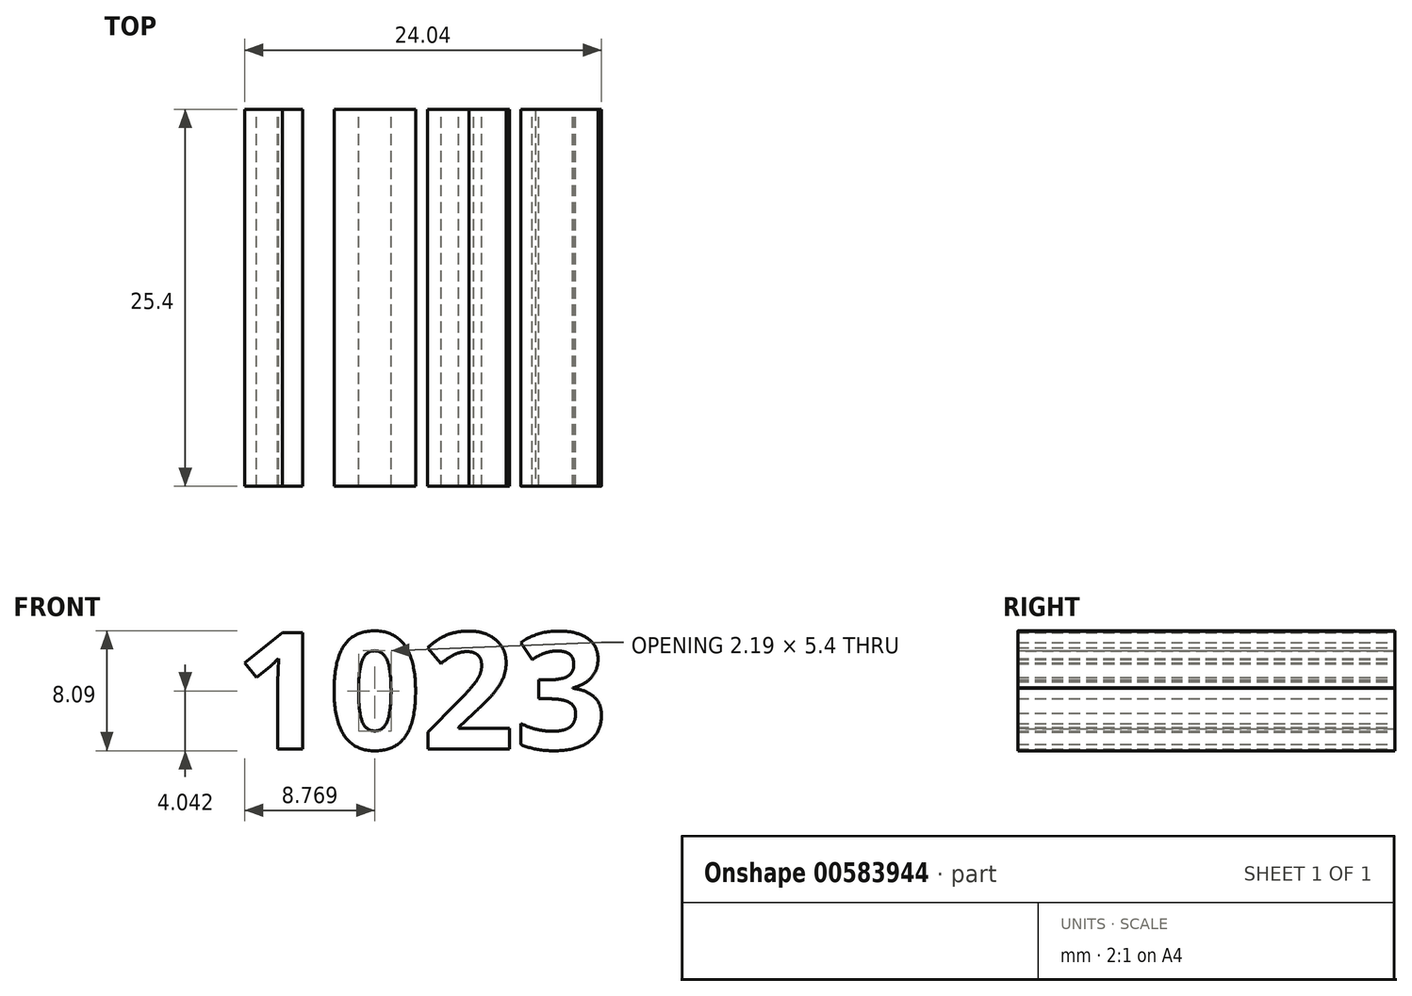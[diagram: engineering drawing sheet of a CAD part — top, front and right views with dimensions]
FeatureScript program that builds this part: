
annotation { "Feature Type Name" : "Feature", "Feature Type Description" : "" }
export const myFeature = defineFeature(function(context is Context, id is Id, definition is map)
    precondition{}
    {
        {
            var Q0;
            Q0=qCreatedBy(makeId("Front.planeOp"),FACE);
            var sketch = newSketch(context, id + "F0", { "sketchPlane" : qUnion([Q0])});
            skText(sketch, "E0", { "text": "1023 ", "fontName": "OpenSans-Bold.ttf"});
            const initialGuessF0  = {"E0": [-0.01475, -0.00554, 1, 0, 0.00792]};
            skSetInitialGuess(sketch, initialGuessF0);
            skSolve(sketch);
        }
        {
            var Q0;
            Q0 = qSketchRegion(id + "F0", true);
            extrude(context, id + "F1", {"entities" : qUnion([Q0]), "depth" : 25.4 * mm, "offsetDistance" : 25.4 * mm});
        }
    });
